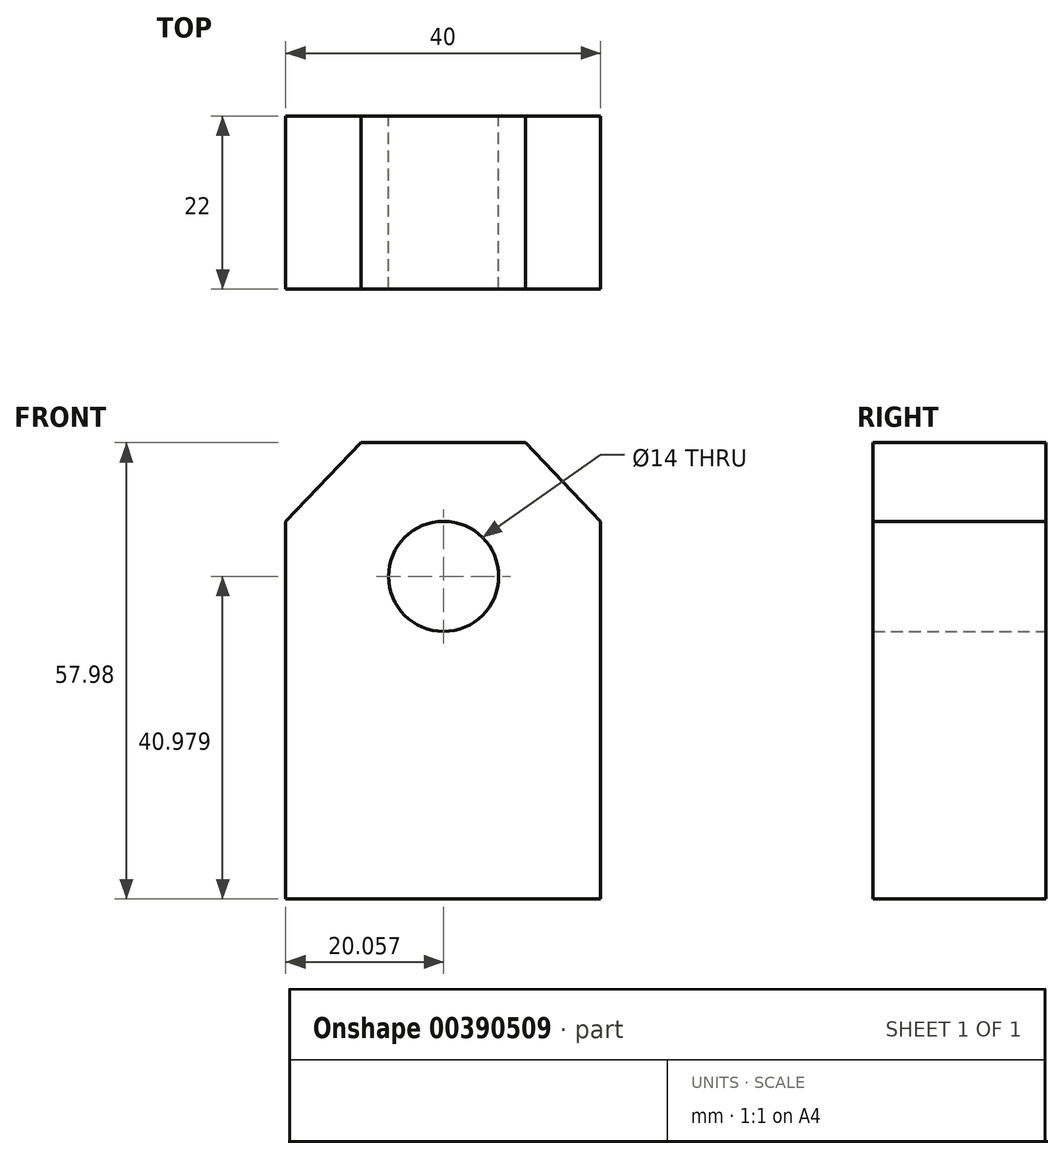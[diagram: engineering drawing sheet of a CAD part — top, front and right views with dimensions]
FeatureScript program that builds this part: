
annotation { "Feature Type Name" : "Feature", "Feature Type Description" : "" }
export const myFeature = defineFeature(function(context is Context, id is Id, definition is map)
    precondition{}
    {
        {
            var Q0;
            Q0=qCreatedBy(makeId("Front.planeOp"),FACE);
            var sketch = newSketch(context, id + "F0", { "sketchPlane" : qUnion([Q0])});
            skLineSegment(sketch, "E0.bottom", {"start": v(10.46, 29) * mm, "end": v(-10.46, 29) * mm});
            skLineSegment(sketch, "E0.top", {"start": v(20, -29) * mm, "end": v(-20, -29) * mm});
            skLineSegment(sketch, "E0.left", {"start": v(20, 18.99) * mm, "end": v(20, -29) * mm});
            skLineSegment(sketch, "E0.right", {"start": v(-20, 18.99) * mm, "end": v(-20, -29) * mm});
            skPoint(sketch, "E0.middle", {"position": v(0, 0) * mm});
            skPoint(sketch, "E1", {"position": v(20, 18.99) * mm});
            skLineSegment(sketch, "E2", {"start": v(20, 18.99) * mm, "end": v(10.46, 29) * mm});
            skCircle(sketch, "E3", {"center": v(0.06, 11.99) * mm, "radius": 7 * mm});
            skPoint(sketch, "E3.first.point", {"position": v(0, 18.99) * mm});
            skPoint(sketch, "E3.second.point", {"position": v(0, 5) * mm});
            skPoint(sketch, "E3.second.point.positionSnap0", {"position": v(0, 18.99) * mm});
            skPoint(sketch, "E3.third.point", {"position": v(-1.3, 5.12) * mm});
            skLineSegment(sketch, "E4.MirrorCS", {"start": v(-20, 18.99) * mm, "end": v(-10.46, 29) * mm});
            skSolve(sketch);
        }
        {
            var Q0;
            Q0=qSketchRegion(id+"F0",true);
            extrude(context, id + "F1", {"entities" : qUnion([Q0]), "depth" : 22 * mm});
        }
    });
